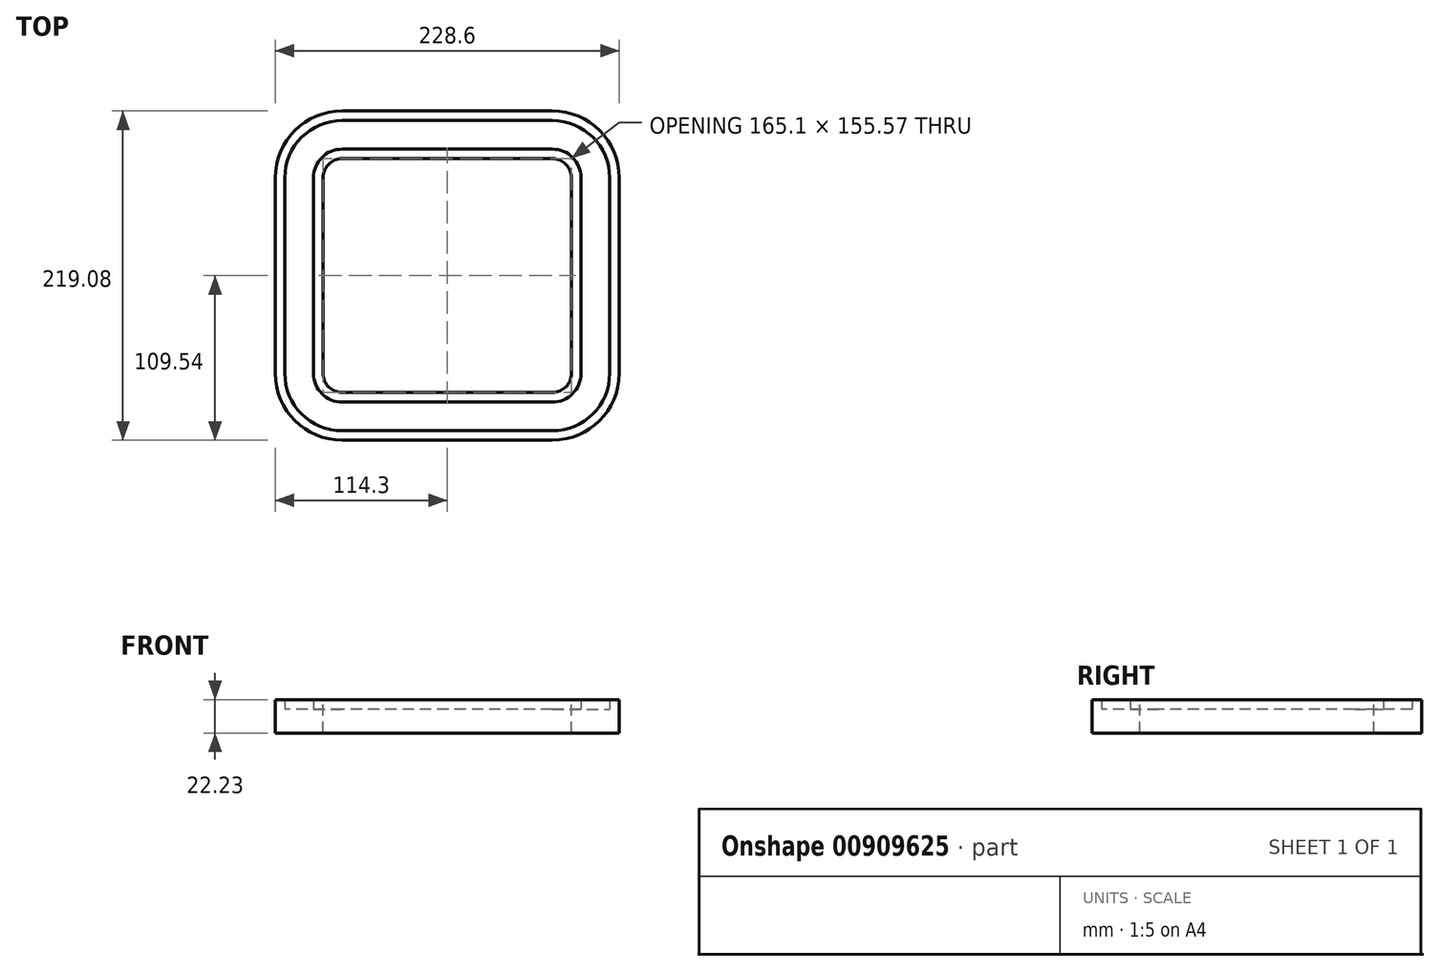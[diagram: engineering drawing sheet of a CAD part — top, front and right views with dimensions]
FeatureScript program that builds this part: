
annotation { "Feature Type Name" : "Feature", "Feature Type Description" : "" }
export const myFeature = defineFeature(function(context is Context, id is Id, definition is map)
    precondition{}
    {
        {
            var Q0;
            Q0=qCreatedBy(makeId("Top.planeOp"),FACE);
            var sketch = newSketch(context, id + "F0", { "sketchPlane" : qUnion([Q0])});
            skLineSegment(sketch, "E0.bottom", {"start": v(69.85, 77.79) * mm, "end": v(-69.85, 77.79) * mm});
            skLineSegment(sketch, "E0.top", {"start": v(69.85, -77.79) * mm, "end": v(-69.85, -77.79) * mm});
            skLineSegment(sketch, "E0.left", {"start": v(82.55, 65.09) * mm, "end": v(82.55, -65.09) * mm});
            skLineSegment(sketch, "E0.right", {"start": v(-82.55, 65.09) * mm, "end": v(-82.55, -65.09) * mm});
            skPoint(sketch, "E0.middle", {"position": v(0, 0) * mm});
            skPoint(sketch, "E1.visualSharp", {"position": v(-82.55, 77.79) * mm});
            skArc(sketch, "E1.filletArc", {"start": v(-69.85, 77.79) * mm, "mid": v(-78.83, 74.07) * mm, "end": v(-82.55, 65.09) * mm});
            skPoint(sketch, "E2.visualSharp", {"position": v(82.55, 77.79) * mm});
            skArc(sketch, "E2.filletArc", {"start": v(82.55, 65.09) * mm, "mid": v(78.83, 74.07) * mm, "end": v(69.85, 77.79) * mm});
            skPoint(sketch, "E3.visualSharp", {"position": v(82.55, -77.79) * mm});
            skArc(sketch, "E3.filletArc", {"start": v(69.85, -77.79) * mm, "mid": v(78.83, -74.07) * mm, "end": v(82.55, -65.09) * mm});
            skPoint(sketch, "E4.visualSharp", {"position": v(-82.55, -77.79) * mm});
            skArc(sketch, "E4.filletArc", {"start": v(-82.55, -65.09) * mm, "mid": v(-78.83, -74.07) * mm, "end": v(-69.85, -77.79) * mm});
            skLineSegment(sketch, "E5.0", {"start": v(-114.3, 65.09) * mm, "end": v(-114.3, -65.09) * mm});
            skArc(sketch, "E5.1", {"start": v(-69.85, 109.54) * mm, "mid": v(-101.28, 96.52) * mm, "end": v(-114.3, 65.09) * mm});
            skArc(sketch, "E5.2", {"start": v(-114.3, -65.09) * mm, "mid": v(-101.28, -96.52) * mm, "end": v(-69.85, -109.54) * mm});
            skLineSegment(sketch, "E5.3", {"start": v(69.85, 109.54) * mm, "end": v(-69.85, 109.54) * mm});
            skLineSegment(sketch, "E5.4", {"start": v(69.85, -109.54) * mm, "end": v(-69.85, -109.54) * mm});
            skArc(sketch, "E5.5", {"start": v(69.85, -109.54) * mm, "mid": v(101.28, -96.52) * mm, "end": v(114.3, -65.09) * mm});
            skLineSegment(sketch, "E5.6", {"start": v(114.3, 65.09) * mm, "end": v(114.3, -65.09) * mm});
            skArc(sketch, "E5.7", {"start": v(114.3, 65.09) * mm, "mid": v(101.28, 96.52) * mm, "end": v(69.85, 109.54) * mm});
            skArc(sketch, "E6.0", {"start": v(-69.85, 84.14) * mm, "mid": v(-83.32, 78.56) * mm, "end": v(-88.9, 65.09) * mm});
            skLineSegment(sketch, "E6.1", {"start": v(69.85, 84.14) * mm, "end": v(-69.85, 84.14) * mm});
            skLineSegment(sketch, "E6.2", {"start": v(-88.9, 65.09) * mm, "end": v(-88.9, -65.09) * mm});
            skArc(sketch, "E6.3", {"start": v(88.9, 65.09) * mm, "mid": v(83.32, 78.56) * mm, "end": v(69.85, 84.14) * mm});
            skArc(sketch, "E6.4", {"start": v(-88.9, -65.09) * mm, "mid": v(-83.32, -78.56) * mm, "end": v(-69.85, -84.14) * mm});
            skLineSegment(sketch, "E6.5", {"start": v(69.85, -84.14) * mm, "end": v(-69.85, -84.14) * mm});
            skArc(sketch, "E6.6", {"start": v(69.85, -84.14) * mm, "mid": v(83.32, -78.56) * mm, "end": v(88.9, -65.09) * mm});
            skLineSegment(sketch, "E6.7", {"start": v(88.9, 65.09) * mm, "end": v(88.9, -65.09) * mm});
            skLineSegment(sketch, "E7.0", {"start": v(69.85, 103.19) * mm, "end": v(-69.85, 103.19) * mm});
            skArc(sketch, "E7.1", {"start": v(107.95, 65.09) * mm, "mid": v(96.8, 92.03) * mm, "end": v(69.85, 103.19) * mm});
            skArc(sketch, "E7.2", {"start": v(-69.85, 103.19) * mm, "mid": v(-96.8, 92.03) * mm, "end": v(-107.95, 65.09) * mm});
            skLineSegment(sketch, "E7.3", {"start": v(107.95, 65.09) * mm, "end": v(107.95, -65.09) * mm});
            skLineSegment(sketch, "E7.4", {"start": v(-107.95, 65.09) * mm, "end": v(-107.95, -65.09) * mm});
            skArc(sketch, "E7.5", {"start": v(-107.95, -65.09) * mm, "mid": v(-96.8, -92.03) * mm, "end": v(-69.85, -103.19) * mm});
            skLineSegment(sketch, "E7.6", {"start": v(69.85, -103.19) * mm, "end": v(-69.85, -103.19) * mm});
            skArc(sketch, "E7.7", {"start": v(69.85, -103.19) * mm, "mid": v(96.8, -92.03) * mm, "end": v(107.95, -65.09) * mm});
            skLineSegment(sketch, "E8.0", {"start": v(-107.19, 65.09) * mm, "end": v(-107.19, -65.09) * mm});
            skArc(sketch, "E8.1", {"start": v(-69.85, 102.43) * mm, "mid": v(-96.25, 91.49) * mm, "end": v(-107.19, 65.09) * mm});
            skArc(sketch, "E8.2", {"start": v(-107.19, -65.09) * mm, "mid": v(-96.25, -91.49) * mm, "end": v(-69.85, -102.43) * mm});
            skLineSegment(sketch, "E8.3", {"start": v(69.85, 102.43) * mm, "end": v(-69.85, 102.43) * mm});
            skLineSegment(sketch, "E8.4", {"start": v(69.85, -102.43) * mm, "end": v(-69.85, -102.43) * mm});
            skArc(sketch, "E8.5", {"start": v(69.85, -102.43) * mm, "mid": v(96.25, -91.49) * mm, "end": v(107.19, -65.09) * mm});
            skLineSegment(sketch, "E8.6", {"start": v(107.19, 65.09) * mm, "end": v(107.19, -65.09) * mm});
            skArc(sketch, "E8.7", {"start": v(107.19, 65.09) * mm, "mid": v(96.25, 91.49) * mm, "end": v(69.85, 102.43) * mm});
            skLineSegment(sketch, "E9.0", {"start": v(-89.66, 65.09) * mm, "end": v(-89.66, -65.09) * mm});
            skArc(sketch, "E9.1", {"start": v(-69.85, 84.9) * mm, "mid": v(-83.86, 79.1) * mm, "end": v(-89.66, 65.09) * mm});
            skArc(sketch, "E9.2", {"start": v(-89.66, -65.09) * mm, "mid": v(-83.86, -79.1) * mm, "end": v(-69.85, -84.9) * mm});
            skLineSegment(sketch, "E9.3", {"start": v(69.85, 84.9) * mm, "end": v(-69.85, 84.9) * mm});
            skLineSegment(sketch, "E9.4", {"start": v(69.85, -84.9) * mm, "end": v(-69.85, -84.9) * mm});
            skArc(sketch, "E9.5", {"start": v(69.85, -84.9) * mm, "mid": v(83.86, -79.1) * mm, "end": v(89.66, -65.09) * mm});
            skLineSegment(sketch, "E9.6", {"start": v(89.66, 65.09) * mm, "end": v(89.66, -65.09) * mm});
            skArc(sketch, "E9.7", {"start": v(89.66, 65.09) * mm, "mid": v(83.86, 79.1) * mm, "end": v(69.85, 84.9) * mm});
            skSolve(sketch);
        }
        {
            var Q0;
            Q0=makeQuery(id+"F0.imprint","IMPRINT",FACE,{"disambiguationData":[TD([[makeQuery(id+"F0.imprint","IMPRINT",EDGE,{"derivedFrom":sQuery(id+"F0.wireOp",EDGE,"E6.0")}),-1.0]])]});
            var Q1;
            Q1=makeQuery(id+"F0.imprint","IMPRINT",FACE,{"disambiguationData":[TD([[makeQuery(id+"F0.imprint","IMPRINT",EDGE,{"derivedFrom":sQuery(id+"F0.wireOp",EDGE,"E5.0")}),1.0]])]});
            var Q2;
            Q2=makeQuery(id+"F0.imprint","IMPRINT",FACE,{"disambiguationData":[TD([[makeQuery(id+"F0.imprint","IMPRINT",EDGE,{"derivedFrom":sQuery(id+"F0.wireOp",EDGE,"E0.bottom")}),-1.0]])]});
            var Q3;
            Q3=makeQuery(id+"F0.imprint","IMPRINT",FACE,{"disambiguationData":[TD([[makeQuery(id+"F0.imprint","IMPRINT",EDGE,{"derivedFrom":sQuery(id+"F0.wireOp",EDGE,"E8.0")}),1.0]])]});
            var Q4;
            Q4=makeQuery(id+"F0.imprint","IMPRINT",FACE,{"disambiguationData":[TD([[makeQuery(id+"F0.imprint","IMPRINT",EDGE,{"derivedFrom":sQuery(id+"F0.wireOp",EDGE,"E7.0")}),1.0]])]});
            extrude(context, id + "F1", {"entities" : qUnion([Q0, Q1, Q2, Q3, Q4]), "oppositeDirection" : true, "depth" : 15.88 * mm, "offsetDistance" : 25.4 * mm});
        }
        {
            var Q0;
            Q0=makeQuery(id+"F0.imprint","IMPRINT",FACE,{"disambiguationData":[TD([[makeQuery(id+"F0.imprint","IMPRINT",EDGE,{"derivedFrom":sQuery(id+"F0.wireOp",EDGE,"E7.0")}),1.0]])]});
            var Q1;
            Q1=makeQuery(id+"F0.imprint","IMPRINT",FACE,{"disambiguationData":[TD([[makeQuery(id+"F0.imprint","IMPRINT",EDGE,{"derivedFrom":sQuery(id+"F0.wireOp",EDGE,"E8.0")}),1.0]])]});
            extrude(context, id + "F2", {"entities" : qUnion([Q0, Q1]), "operationType" : NewBodyOperationType.REMOVE, "depth" : 9.52 * mm, "offsetDistance" : 25.4 * mm});
        }
        {
            var Q0;
            Q0=makeQuery(id+"F0.imprint","IMPRINT",FACE,{"disambiguationData":[TD([[makeQuery(id+"F0.imprint","IMPRINT",EDGE,{"derivedFrom":sQuery(id+"F0.wireOp",EDGE,"E5.0")}),1.0]])]});
            var Q1;
            Q1=makeQuery(id+"F0.imprint","IMPRINT",FACE,{"disambiguationData":[TD([[makeQuery(id+"F0.imprint","IMPRINT",EDGE,{"derivedFrom":sQuery(id+"F0.wireOp",EDGE,"E0.bottom")}),-1.0]])]});
            extrude(context, id + "F3", {"entities" : qUnion([Q0, Q1]), "operationType" : NewBodyOperationType.ADD, "depth" : 6.35 * mm, "offsetDistance" : 25.4 * mm});
        }
    });
